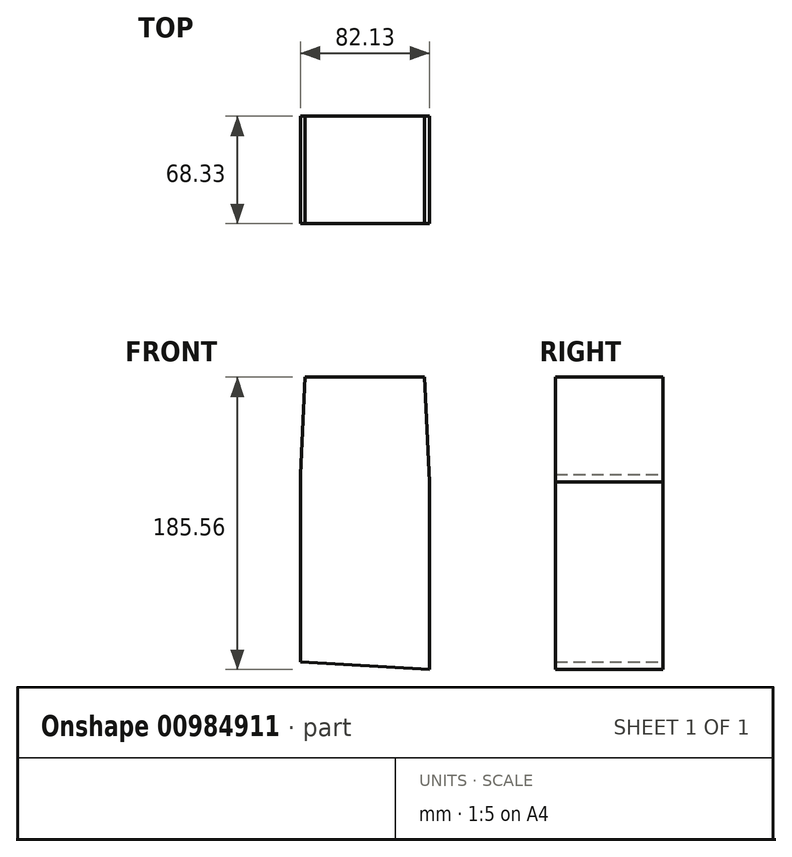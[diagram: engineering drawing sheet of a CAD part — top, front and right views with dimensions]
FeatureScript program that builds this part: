
annotation { "Feature Type Name" : "Feature", "Feature Type Description" : "" }
export const myFeature = defineFeature(function(context is Context, id is Id, definition is map)
    precondition{}
    {
        {
            var Q0;
            Q0=qCreatedBy(makeId("Front.planeOp"),FACE);
            var sketch = newSketch(context, id + "F0", { "sketchPlane" : qUnion([Q0])});
            skLineSegment(sketch, "E0", {"start": v(36.52, 29.16) * mm, "end": v(-39.31, 29.16) * mm});
            skLineSegment(sketch, "E1", {"start": v(-39.31, 29.16) * mm, "end": v(-42.4, -32.59) * mm});
            skLineSegment(sketch, "E2", {"start": v(-42.4, -32.59) * mm, "end": v(39.73, -37.42) * mm});
            skLineSegment(sketch, "E3", {"start": v(39.73, -37.42) * mm, "end": v(36.52, 29.16) * mm});
            skSolve(sketch);
        }
        {
            var Q0;
            Q0 = qSketchRegion(id + "F0", true);
            extrude(context, id + "F1", {"entities" : qUnion([Q0]), "depth" : 25.4 * mm, "offsetDistance" : 25.4 * mm});
        }
        {
            var Q0;
            Q0=makeQuery(id+"F1.opExtrude","CAP_FACE",FACE,{"disambiguationData":[OSD([sQuery(id+"F0.wireOp",EDGE,"E0"),sQuery(id+"F0.wireOp",EDGE,"E1"),sQuery(id+"F0.wireOp",EDGE,"E2"),sQuery(id+"F0.wireOp",EDGE,"E3")])],"isStart":false});
            extrude(context, id + "F2", {"entities" : qUnion([Q0]), "operationType" : NewBodyOperationType.ADD, "depth" : 42.93 * mm, "offsetDistance" : 25.4 * mm});
        }
        {
            var Q0;
            {var subQ0=sQuery(id+"F0.wireOp",EDGE,"E0");Q0=makeQuery(id+"F2.boolean.opBoolean","MERGE",FACE,{"derivedFrom":[makeQuery(id+"F1.opExtrude","SWEPT_FACE",FACE,{"disambiguationData":[OSD([subQ0])]}),makeQuery(id+"F2.opExtrude","SWEPT_FACE",FACE,{"disambiguationData":[OSD([subQ0])]})]});}
            var Q1;
            {var subQ0=sQuery(id+"F0.wireOp",EDGE,"E3");Q1=makeQuery(id+"F2.boolean.opBoolean","MERGE",FACE,{"derivedFrom":[makeQuery(id+"F1.opExtrude","SWEPT_FACE",FACE,{"disambiguationData":[OSD([subQ0])]}),makeQuery(id+"F2.opExtrude","SWEPT_FACE",FACE,{"disambiguationData":[OSD([subQ0])]})]});}
            var Q2;
            {var subQ0=sQuery(id+"F0.wireOp",EDGE,"E2");Q2=makeQuery(id+"F2.boolean.opBoolean","MERGE",FACE,{"derivedFrom":[makeQuery(id+"F1.opExtrude","SWEPT_FACE",FACE,{"disambiguationData":[OSD([subQ0])]}),makeQuery(id+"F2.opExtrude","SWEPT_FACE",FACE,{"disambiguationData":[OSD([subQ0])]})]});}
            extrude(context, id + "F3", {"entities" : qUnion([Q0, Q1, Q2]), "operationType" : NewBodyOperationType.ADD, "oppositeDirection" : true, "depth" : 118.98 * mm, "offsetDistance" : 25.4 * mm});
        }
        {
            var Q0;
            Q0=makeQuery(id+"F3.opExtrude","SWEPT_FACE",FACE,{"disambiguationData":[OSD([sQuery(id+"F0.wireOp",EDGE,"E2"),sQuery(id+"F0.wireOp",EDGE,"E3")]),OD(0.0)]});
            var sketch = newSketch(context, id + "F4", { "sketchPlane" : qUnion([Q0])});
            skCircle(sketch, "E4", {"center": v(-34.03, -93.8) * mm, "radius": 12.97 * mm});
            skSolve(sketch);
        }
        {
            var Q0;
            Q0=sQuery(id+"F4.wireOp",EDGE,"E4");
            extrude(context, id + "F5", {"bodyType" : ToolBodyType.SURFACE, "surfaceEntities" : qUnion([Q0]), "oppositeDirection" : true, "depth" : 97.93 * mm, "offsetDistance" : 25.4 * mm});
        }
        {
            var Q0;
            Q0=makeQuery(id+"F3.opExtrude","SWEPT_FACE",FACE,{"disambiguationData":[OSD([sQuery(id+"F0.wireOp",EDGE,"E1"),sQuery(id+"F0.wireOp",EDGE,"E2")])]});
            var sketch = newSketch(context, id + "F6", { "sketchPlane" : qUnion([Q0])});
            skCircle(sketch, "E5", {"center": v(40.02, -64.16) * mm, "radius": 9.54 * mm});
            skSolve(sketch);
        }
        {
            var Q0;
            Q0=sQuery(id+"F6.wireOp",EDGE,"E5");
            extrude(context, id + "F7", {"bodyType" : ToolBodyType.SURFACE, "surfaceEntities" : qUnion([Q0]), "depth" : 25.4 * mm, "offsetDistance" : 25.4 * mm});
        }
    });
